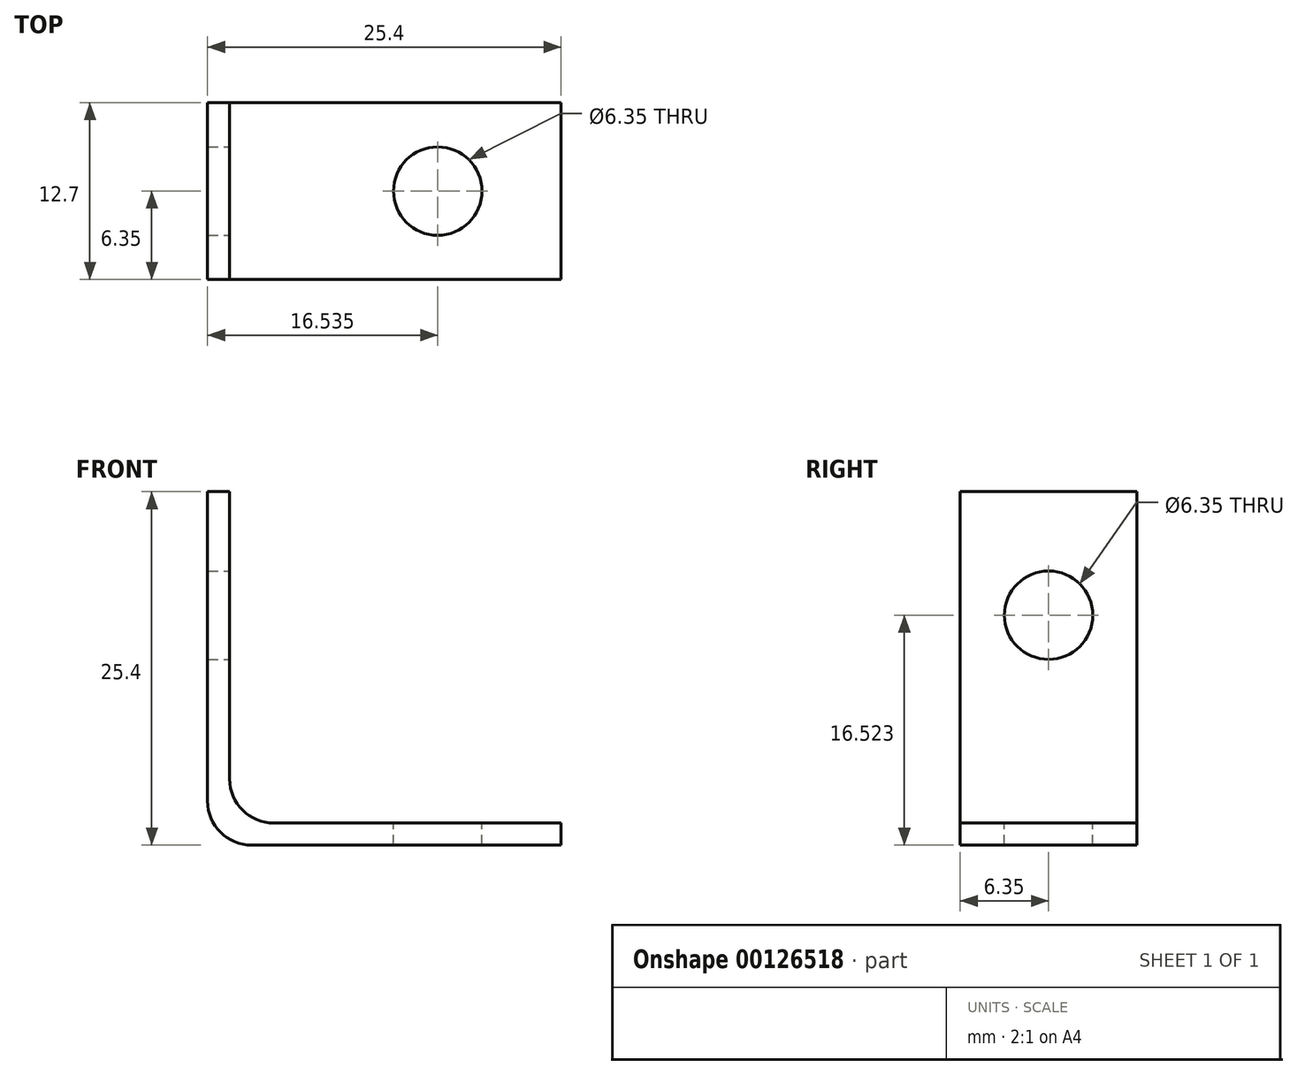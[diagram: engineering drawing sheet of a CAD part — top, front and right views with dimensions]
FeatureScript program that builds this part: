
annotation { "Feature Type Name" : "Feature", "Feature Type Description" : "" }
export const myFeature = defineFeature(function(context is Context, id is Id, definition is map)
    precondition{}
    {
        {
            var Q0;
            Q0=qCreatedBy(makeId("Front.planeOp"),FACE);
            var sketch = newSketch(context, id + "F0", { "sketchPlane" : qUnion([Q0])});
            skLineSegment(sketch, "E0", {"start": v(0, 25.4) * mm, "end": v(0, 3.18) * mm});
            skLineSegment(sketch, "E1", {"start": v(3.18, 0) * mm, "end": v(25.4, 0) * mm});
            skLineSegment(sketch, "E2", {"start": v(0, 25.4) * mm, "end": v(1.59, 25.4) * mm});
            skLineSegment(sketch, "E3", {"start": v(1.59, 25.4) * mm, "end": v(1.59, 4.76) * mm});
            skLineSegment(sketch, "E4", {"start": v(25.4, 0) * mm, "end": v(25.4, 1.59) * mm});
            skLineSegment(sketch, "E5", {"start": v(25.4, 1.59) * mm, "end": v(4.76, 1.59) * mm});
            skArc(sketch, "E6.filletArc", {"start": v(1.59, 4.76) * mm, "mid": v(2.52, 2.52) * mm, "end": v(4.76, 1.59) * mm});
            skPoint(sketch, "E7.visualSharp", {"position": v(0, 0) * mm});
            skArc(sketch, "E7.filletArc", {"start": v(0, 3.18) * mm, "mid": v(0.93, 0.93) * mm, "end": v(3.18, 0) * mm});
            skSolve(sketch);
        }
        {
            var Q0;
            Q0=makeQuery(id+"F0.imprint","IMPRINT",FACE,{"disambiguationData":[TD([[makeQuery(id+"F0.imprint","IMPRINT",EDGE,{"derivedFrom":sQuery(id+"F0.wireOp",EDGE,"E0")}),1.0]])]});
            extrude(context, id + "F1", {"entities" : qUnion([Q0]), "endBound" : BoundingType.SYMMETRIC, "depth" : 12.7 * mm});
        }
        {
            var Q0;
            Q0=makeQuery(id+"F1.opExtrude","SWEPT_FACE",FACE,{"disambiguationData":[OSD([sQuery(id+"F0.wireOp",EDGE,"E3")])]});
            var sketch = newSketch(context, id + "F2", { "sketchPlane" : qUnion([Q0])});
            skCircle(sketch, "E8", {"center": v(0, 16.52) * mm, "radius": 3.18 * mm});
            skSolve(sketch);
        }
        {
            var Q0;
            Q0=makeQuery(id+"F2.imprint","IMPRINT",FACE,{"disambiguationData":[TD([[makeQuery(id+"F2.imprint","IMPRINT",EDGE,{"derivedFrom":sQuery(id+"F2.wireOp",EDGE,"E8")}),1.0]])]});
            extrude(context, id + "F3", {"entities" : qUnion([Q0]), "operationType" : NewBodyOperationType.REMOVE, "endBound" : BoundingType.THROUGH_ALL, "oppositeDirection" : true, "depth" : 25.4 * mm});
        }
        {
            var Q0;
            Q0=makeQuery(id+"F1.opExtrude","SWEPT_FACE",FACE,{"disambiguationData":[OSD([sQuery(id+"F0.wireOp",EDGE,"E5")])]});
            var sketch = newSketch(context, id + "F4", { "sketchPlane" : qUnion([Q0])});
            skCircle(sketch, "E9", {"center": v(16.54, 0) * mm, "radius": 3.18 * mm});
            skSolve(sketch);
        }
        {
            var Q0;
            Q0 = qSketchRegion(id + "F4", true);
            extrude(context, id + "F5", {"entities" : qUnion([Q0]), "operationType" : NewBodyOperationType.REMOVE, "endBound" : BoundingType.THROUGH_ALL, "oppositeDirection" : true, "depth" : 25.4 * mm});
        }
    });
